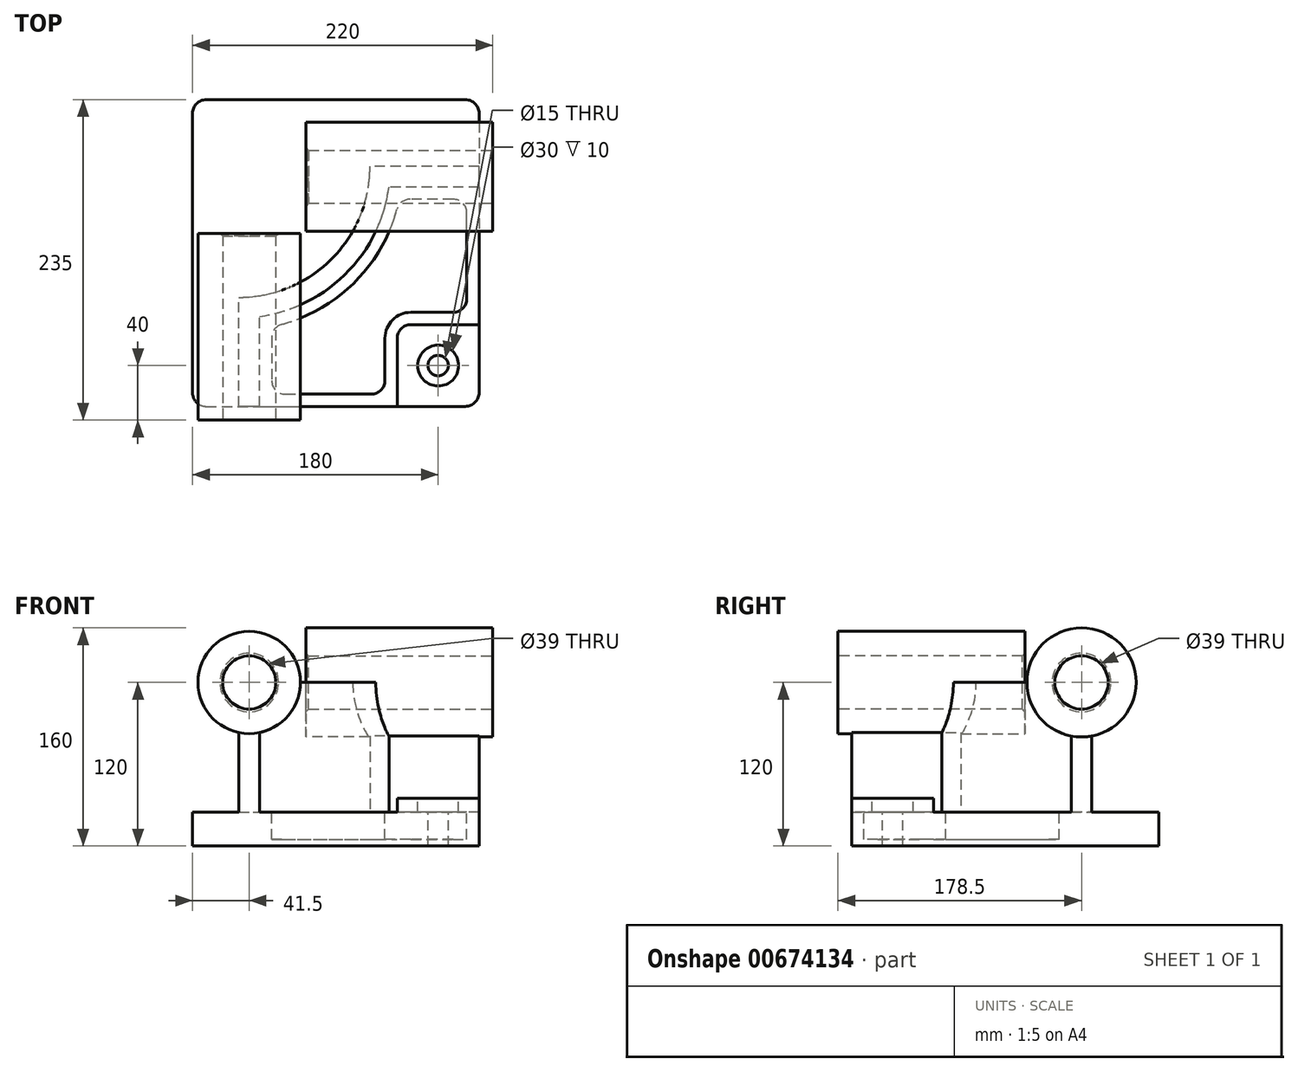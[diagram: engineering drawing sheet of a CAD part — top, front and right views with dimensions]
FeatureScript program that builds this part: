
annotation { "Feature Type Name" : "Feature", "Feature Type Description" : "" }
export const myFeature = defineFeature(function(context is Context, id is Id, definition is map)
    precondition{}
    {
        {
            var Q0;
            Q0=qCreatedBy(makeId("Top.planeOp"),FACE);
            var sketch = newSketch(context, id + "F0", { "sketchPlane" : qUnion([Q0])});
            skLineSegment(sketch, "E0.bottom", {"start": v(-105, 112.5) * mm, "end": v(105, 112.5) * mm});
            skLineSegment(sketch, "E0.top", {"start": v(-105, -112.5) * mm, "end": v(105, -112.5) * mm});
            skLineSegment(sketch, "E0.left", {"start": v(-105, 112.5) * mm, "end": v(-105, -112.5) * mm});
            skLineSegment(sketch, "E0.right", {"start": v(105, 112.5) * mm, "end": v(105, -112.5) * mm});
            skPoint(sketch, "E0.middle", {"position": v(0, 0) * mm});
            skSolve(sketch);
        }
        {
            var Q0;
            Q0=makeQuery(id+"F0.imprint","IMPRINT",FACE,{"disambiguationData":[TD([[makeQuery(id+"F0.imprint","IMPRINT",EDGE,{"derivedFrom":sQuery(id+"F0.wireOp",EDGE,"E0.bottom")}),-1.0]])]});
            extrude(context, id + "F1", {"entities" : qUnion([Q0]), "depth" : 25 * mm, "offsetDistance" : 25 * mm});
        }
        {
            var Q0;
            Q0=makeQuery(id+"F1.opExtrude","CAP_FACE",FACE,{"disambiguationData":[OSD([sQuery(id+"F0.wireOp",EDGE,"E0.bottom"),sQuery(id+"F0.wireOp",EDGE,"E0.top"),sQuery(id+"F0.wireOp",EDGE,"E0.left"),sQuery(id+"F0.wireOp",EDGE,"E0.right")])],"isStart":false});
            var sketch = newSketch(context, id + "F2", { "sketchPlane" : qUnion([Q0])});
            skLineSegment(sketch, "E1", {"start": v(-71, -112.5) * mm, "end": v(-71, -32.5) * mm});
            skLineSegment(sketch, "E2", {"start": v(105, 63.5) * mm, "end": v(25, 63.5) * mm});
            skArc(sketch, "E3", {"start": v(-71, -32.5) * mm, "mid": v(-3.12, -4.38) * mm, "end": v(25, 63.5) * mm});
            skLineSegment(sketch, "E4", {"start": v(-71, 63.5) * mm, "end": v(25, 63.5) * mm, "construction": true});
            skLineSegment(sketch, "E5", {"start": v(-71, 63.5) * mm, "end": v(-71, -32.5) * mm, "construction": true});
            skLineSegment(sketch, "E6.0", {"start": v(-56, -112.5) * mm, "end": v(-56, -46.48) * mm});
            skArc(sketch, "E6.1", {"start": v(-56, -46.48) * mm, "mid": v(7.49, -14.99) * mm, "end": v(38.98, 48.5) * mm});
            skLineSegment(sketch, "E6.2", {"start": v(105, 48.5) * mm, "end": v(38.98, 48.5) * mm});
            skLineSegment(sketch, "E7.0", {"start": v(105, 112.5) * mm, "end": v(105, -112.5) * mm});
            skLineSegment(sketch, "E8.0", {"start": v(-105, -112.5) * mm, "end": v(105, -112.5) * mm});
            skSolve(sketch);
        }
        {
            var Q0;
            {var subQ2=sQuery(id+"F2.wireOp",EDGE,"E1");Q0=makeQuery(id+"F2.imprint","IMPRINT",FACE,{"disambiguationData":[TD([[makeQuery(id+"F2.imprint","IMPRINT",EDGE,{"derivedFrom":subQ2}),-1.0]])]});}
            extrude(context, id + "F3", {"entities" : qUnion([Q0]), "operationType" : NewBodyOperationType.ADD, "depth" : 95 * mm, "offsetDistance" : 25 * mm});
        }
        {
            var Q0;
            Q0=makeQuery(id+"F3.boolean.opBoolean","MERGE",FACE,{"derivedFrom":[makeQuery(id+"F1.opExtrude","SWEPT_FACE",FACE,{"disambiguationData":[OSD([sQuery(id+"F0.wireOp",EDGE,"E0.top")])]}),makeQuery(id+"F3.opExtrude","SWEPT_FACE",FACE,{"disambiguationData":[OSD([sQuery(id+"F2.wireOp",EDGE,"E8.0")])]})]});
            var sketch = newSketch(context, id + "F4", { "sketchPlane" : qUnion([Q0])});
            skCircle(sketch, "E9", {"center": v(-63.5, 120) * mm, "radius": 37.5 * mm});
            skSolve(sketch);
        }
        {
            var Q0;
            Q0 = qSketchRegion(id + "F4", true);
            extrude(context, id + "F5", {"entities" : qUnion([Q0]), "operationType" : NewBodyOperationType.ADD, "depth" : 10 * mm, "offsetDistance" : 25 * mm, "hasSecondDirection" : true, "secondDirectionOppositeDirection" : true, "secondDirectionDepth" : (137 - 10) * mm});
        }
        {
            var Q0;
            Q0=makeQuery(id+"F3.boolean.opBoolean","MERGE",FACE,{"derivedFrom":[makeQuery(id+"F1.opExtrude","SWEPT_FACE",FACE,{"disambiguationData":[OSD([sQuery(id+"F0.wireOp",EDGE,"E0.right")])]}),makeQuery(id+"F3.opExtrude","SWEPT_FACE",FACE,{"disambiguationData":[OSD([sQuery(id+"F2.wireOp",EDGE,"E7.0")])]})]});
            var sketch = newSketch(context, id + "F6", { "sketchPlane" : qUnion([Q0])});
            skCircle(sketch, "E10", {"center": v(56, 120) * mm, "radius": 40 * mm});
            skSolve(sketch);
        }
        {
            var Q0;
            Q0 = qSketchRegion(id + "F6", true);
            extrude(context, id + "F7", {"entities" : qUnion([Q0]), "operationType" : NewBodyOperationType.ADD, "depth" : 10 * mm, "offsetDistance" : 25 * mm, "hasSecondDirection" : true, "secondDirectionOppositeDirection" : true, "secondDirectionDepth" : (137 - 10) * mm});
        }
        {
            var Q0;
            {var subQ0=sQuery(id+"F0.wireOp",EDGE,"E0.right");var subQ1=sQuery(id+"F0.wireOp",EDGE,"E0.top");Q0=makeQuery(id+"F3.boolean.opBoolean","SPLIT",FACE,{"disambiguationData":[TD([makeQuery(id+"F3.opExtrude","SWEPT_FACE",FACE,{"disambiguationData":[OSD([sQuery(id+"F2.wireOp",EDGE,"E6.0")])]})])],"derivedFrom":makeQuery(id+"F1.opExtrude","CAP_FACE",FACE,{"disambiguationData":[OSD([sQuery(id+"F0.wireOp",EDGE,"E0.bottom"),subQ1,sQuery(id+"F0.wireOp",EDGE,"E0.left"),subQ0])],"isStart":false})});}
            var sketch = newSketch(context, id + "F8", { "sketchPlane" : qUnion([Q0])});
            skLineSegment(sketch, "E11.bottom", {"start": v(105, -112.5) * mm, "end": v(45, -112.5) * mm});
            skLineSegment(sketch, "E11.top", {"start": v(105, -52.5) * mm, "end": v(45, -52.5) * mm});
            skLineSegment(sketch, "E11.left", {"start": v(105, -112.5) * mm, "end": v(105, -52.5) * mm});
            skLineSegment(sketch, "E11.right", {"start": v(45, -112.5) * mm, "end": v(45, -52.5) * mm});
            skSolve(sketch);
        }
        {
            var Q0;
            Q0=makeQuery(id+"F8.imprint","IMPRINT",FACE,{"disambiguationData":[TD([[makeQuery(id+"F8.imprint","IMPRINT",EDGE,{"derivedFrom":sQuery(id+"F8.wireOp",EDGE,"E11.bottom")}),1.0]])]});
            extrude(context, id + "F9", {"entities" : qUnion([Q0]), "operationType" : NewBodyOperationType.ADD, "depth" : (35 - 25) * mm, "offsetDistance" : 25 * mm});
        }
        {
            var Q0;
            Q0=makeQuery(id+"F9.opExtrude","SWEPT_EDGE",EDGE,{"disambiguationData":[OSD([sQuery(id+"F8.wireOp",EDGE,"E11.top"),sQuery(id+"F8.wireOp",EDGE,"E11.right")])]});
            fillet(context, id + "F10", {"entities" : qUnion([Q0]), "radius" : 10 * mm, "tangentPropagation" : true, "allowEdgeOverflow" : false});
        }
        {
            var Q0;
            {var subQ0=sQuery(id+"F0.wireOp",EDGE,"E0.right");var subQ1=sQuery(id+"F0.wireOp",EDGE,"E0.top");Q0=makeQuery(id+"F3.boolean.opBoolean","SPLIT",FACE,{"disambiguationData":[TD([makeQuery(id+"F3.opExtrude","SWEPT_FACE",FACE,{"disambiguationData":[OSD([sQuery(id+"F2.wireOp",EDGE,"E6.0")])]})])],"derivedFrom":makeQuery(id+"F1.opExtrude","CAP_FACE",FACE,{"disambiguationData":[OSD([sQuery(id+"F0.wireOp",EDGE,"E0.bottom"),subQ1,sQuery(id+"F0.wireOp",EDGE,"E0.left"),subQ0])],"isStart":false})});}
            var sketch = newSketch(context, id + "F11", { "sketchPlane" : qUnion([Q0])});
            skLineSegment(sketch, "E12.0", {"start": v(-47, -54.08) * mm, "end": v(-47, -103.5) * mm});
            skArc(sketch, "E12.1", {"start": v(46.58, 39.5) * mm, "mid": v(13.85, -21.35) * mm, "end": v(-47, -54.08) * mm});
            skLineSegment(sketch, "E12.2", {"start": v(-47, -103.5) * mm, "end": v(36, -103.5) * mm});
            skLineSegment(sketch, "E12.3", {"start": v(96, 39.5) * mm, "end": v(46.58, 39.5) * mm});
            skLineSegment(sketch, "E12.4", {"start": v(36, -103.5) * mm, "end": v(36, -62.5) * mm});
            skArc(sketch, "E12.5", {"start": v(36, -62.5) * mm, "mid": v(41.56, -49.06) * mm, "end": v(55, -43.5) * mm});
            skLineSegment(sketch, "E12.6", {"start": v(55, -43.5) * mm, "end": v(96, -43.5) * mm});
            skLineSegment(sketch, "E12.7", {"start": v(96, -43.5) * mm, "end": v(96, 39.5) * mm});
            skSolve(sketch);
        }
        {
            var Q0;
            Q0=makeQuery(id+"F11.imprint","IMPRINT",FACE,{"disambiguationData":[TD([[makeQuery(id+"F11.imprint","IMPRINT",EDGE,{"derivedFrom":sQuery(id+"F11.wireOp",EDGE,"E12.0")}),1.0]])]});
            extrude(context, id + "F12", {"entities" : qUnion([Q0]), "operationType" : NewBodyOperationType.REMOVE, "oppositeDirection" : true, "depth" : (25 - 5) * mm, "offsetDistance" : 25 * mm});
        }
        {
            var Q0;
            Q0=makeQuery(id+"F9.opExtrude","CAP_FACE",FACE,{"disambiguationData":[OSD([sQuery(id+"F8.wireOp",EDGE,"E11.bottom"),sQuery(id+"F8.wireOp",EDGE,"E11.top"),sQuery(id+"F8.wireOp",EDGE,"E11.left"),sQuery(id+"F8.wireOp",EDGE,"E11.right")])],"isStart":false});
            var sketch = newSketch(context, id + "F13", { "sketchPlane" : qUnion([Q0])});
            skCircle(sketch, "E13", {"center": v(75, -82.5) * mm, "radius": 15 * mm});
            skSolve(sketch);
        }
        {
            var Q0;
            Q0=makeQuery(id+"F12.boolean.opBoolean","COPY",EDGE,{"derivedFrom":makeQuery(id+"F12.opExtrude","SWEPT_EDGE",EDGE,{"disambiguationData":[OSD([sQuery(id+"F11.wireOp",EDGE,"E12.2"),sQuery(id+"F11.wireOp",EDGE,"E12.4")])]})});
            var Q1;
            Q1=makeQuery(id+"F12.boolean.opBoolean","COPY",EDGE,{"derivedFrom":makeQuery(id+"F12.opExtrude","SWEPT_EDGE",EDGE,{"disambiguationData":[OSD([sQuery(id+"F11.wireOp",EDGE,"E12.6"),sQuery(id+"F11.wireOp",EDGE,"E12.7")])]})});
            var Q2;
            Q2=makeQuery(id+"F12.boolean.opBoolean","COPY",EDGE,{"derivedFrom":makeQuery(id+"F12.opExtrude","SWEPT_EDGE",EDGE,{"disambiguationData":[OSD([sQuery(id+"F11.wireOp",EDGE,"E12.1"),sQuery(id+"F11.wireOp",EDGE,"E12.3")])]})});
            var Q3;
            Q3=makeQuery(id+"F12.boolean.opBoolean","COPY",EDGE,{"derivedFrom":makeQuery(id+"F12.opExtrude","SWEPT_EDGE",EDGE,{"disambiguationData":[OSD([sQuery(id+"F11.wireOp",EDGE,"E12.0"),sQuery(id+"F11.wireOp",EDGE,"E12.1")])]})});
            var Q4;
            Q4=makeQuery(id+"F12.boolean.opBoolean","COPY",EDGE,{"derivedFrom":makeQuery(id+"F12.opExtrude","SWEPT_EDGE",EDGE,{"disambiguationData":[OSD([sQuery(id+"F11.wireOp",EDGE,"E12.3"),sQuery(id+"F11.wireOp",EDGE,"E12.7")])]})});
            var Q5;
            Q5=makeQuery(id+"F12.boolean.opBoolean","COPY",EDGE,{"derivedFrom":makeQuery(id+"F12.opExtrude","SWEPT_EDGE",EDGE,{"disambiguationData":[OSD([sQuery(id+"F11.wireOp",EDGE,"E12.0"),sQuery(id+"F11.wireOp",EDGE,"E12.2")])]})});
            fillet(context, id + "F14", {"entities" : qUnion([Q0, Q1, Q2, Q3, Q4, Q5]), "radius" : 10 * mm, "tangentPropagation" : true, "allowEdgeOverflow" : false});
        }
        {
            var Q0;
            Q0=sQuery(id+"F13.wireOp",VERTEX,"E13.center");
            var Q1;
            Q1=makeQuery(id+"F1.opExtrude","SWEPT_BODY",BODY,{"disambiguationData":[OSD([sQuery(id+"F0.wireOp",EDGE,"E0.bottom"),sQuery(id+"F0.wireOp",EDGE,"E0.top"),sQuery(id+"F0.wireOp",EDGE,"E0.left"),sQuery(id+"F0.wireOp",EDGE,"E0.right")])]});
            hole(context, id + "F15", {"style" : HoleStyle.C_BORE, "endStyle" : HoleEndStyle.THROUGH, "holeDiameter" : 15 * mm, "cBoreDiameter" : 30 * mm, "cBoreDepth" : 10 * mm, "majorDiameter" : 5 * mm, "isTappedThrough" : true, "tappedDepth" : 12 * mm, "tapClearance" : 3, "locations" : qUnion([Q0]), "scope" : qUnion([Q1])});
        }
        {
            var Q0;
            Q0=makeQuery(id+"F5.opExtrude","CAP_FACE",FACE,{"disambiguationData":[OSD([sQuery(id+"F4.wireOp",EDGE,"E9")])],"isStart":false});
            var sketch = newSketch(context, id + "F16", { "sketchPlane" : qUnion([Q0])});
            skCircle(sketch, "E14", {"center": v(-63.5, 120) * mm, "radius": 19.5 * mm});
            skSolve(sketch);
        }
        {
            var Q0;
            Q0 = qSketchRegion(id + "F16", true);
            extrude(context, id + "F17", {"entities" : qUnion([Q0]), "operationType" : NewBodyOperationType.REMOVE, "endBound" : BoundingType.THROUGH_ALL, "oppositeDirection" : true, "depth" : 25 * mm, "offsetDistance" : 25 * mm});
        }
        {
            var Q0;
            Q0=makeQuery(id+"F7.opExtrude","CAP_FACE",FACE,{"disambiguationData":[OSD([sQuery(id+"F6.wireOp",EDGE,"E10")])],"isStart":false});
            var sketch = newSketch(context, id + "F18", { "sketchPlane" : qUnion([Q0])});
            skCircle(sketch, "E15", {"center": v(56, 120) * mm, "radius": 19.5 * mm});
            skSolve(sketch);
        }
        {
            var Q0;
            Q0 = qSketchRegion(id + "F18", true);
            extrude(context, id + "F19", {"entities" : qUnion([Q0]), "operationType" : NewBodyOperationType.REMOVE, "endBound" : BoundingType.THROUGH_ALL, "oppositeDirection" : true, "depth" : 25 * mm, "offsetDistance" : 25 * mm});
        }
        {
            var Q0;
            Q0=makeQuery(id+"F17.boolean.opBoolean","COPY",EDGE,{"derivedFrom":makeQuery(id+"F17.opExtrude","CAP_EDGE",EDGE,{"disambiguationData":[OSD([sQuery(id+"F16.wireOp",EDGE,"E14")])],"isStart":true})});
            var Q1;
            Q1=makeQuery(id+"F19.boolean.opBoolean","COPY",EDGE,{"derivedFrom":makeQuery(id+"F19.opExtrude","CAP_EDGE",EDGE,{"disambiguationData":[OSD([sQuery(id+"F18.wireOp",EDGE,"E15")])],"isStart":true})});
            var Q2;
            Q2=makeQuery(id+"F19.boolean.opBoolean","INTERSECT",EDGE,{"derivedFrom":[makeQuery(id+"F7.opExtrude","CAP_FACE",FACE,{"disambiguationData":[OSD([sQuery(id+"F6.wireOp",EDGE,"E10")])],"isStart":true}),makeQuery(id+"F19.opExtrude","SWEPT_FACE",FACE,{"disambiguationData":[OSD([sQuery(id+"F18.wireOp",EDGE,"E15")])]})]});
            var Q3;
            Q3=makeQuery(id+"F17.boolean.opBoolean","INTERSECT",EDGE,{"derivedFrom":[makeQuery(id+"F5.opExtrude","CAP_FACE",FACE,{"disambiguationData":[OSD([sQuery(id+"F4.wireOp",EDGE,"E9")])],"isStart":true}),makeQuery(id+"F17.opExtrude","SWEPT_FACE",FACE,{"disambiguationData":[OSD([sQuery(id+"F16.wireOp",EDGE,"E14")])]})]});
            chamfer(context, id + "F20", {"entities" : qUnion([Q0, Q1, Q2, Q3]), "width" : 2 * mm, "tangentPropagation" : true});
        }
        {
            var Q0;
            Q0=makeQuery(id+"F9.boolean.opBoolean","MERGE",EDGE,{"derivedFrom":[makeQuery(id+"F1.opExtrude","SWEPT_EDGE",EDGE,{"disambiguationData":[OSD([sQuery(id+"F0.wireOp",EDGE,"E0.top"),sQuery(id+"F0.wireOp",EDGE,"E0.right")])]}),makeQuery(id+"F9.opExtrude","SWEPT_EDGE",EDGE,{"disambiguationData":[OSD([sQuery(id+"F8.wireOp",EDGE,"E11.bottom"),sQuery(id+"F8.wireOp",EDGE,"E11.left")])]})]});
            var Q1;
            Q1=makeQuery(id+"F1.opExtrude","SWEPT_EDGE",EDGE,{"disambiguationData":[OSD([sQuery(id+"F0.wireOp",EDGE,"E0.bottom"),sQuery(id+"F0.wireOp",EDGE,"E0.right")])]});
            var Q2;
            Q2=makeQuery(id+"F1.opExtrude","SWEPT_EDGE",EDGE,{"disambiguationData":[OSD([sQuery(id+"F0.wireOp",EDGE,"E0.bottom"),sQuery(id+"F0.wireOp",EDGE,"E0.left")])]});
            var Q3;
            Q3=makeQuery(id+"F1.opExtrude","SWEPT_EDGE",EDGE,{"disambiguationData":[OSD([sQuery(id+"F0.wireOp",EDGE,"E0.top"),sQuery(id+"F0.wireOp",EDGE,"E0.left")])]});
            fillet(context, id + "F21", {"entities" : qUnion([Q0, Q1, Q2, Q3]), "radius" : 10 * mm, "tangentPropagation" : true, "allowEdgeOverflow" : false});
        }
    });
